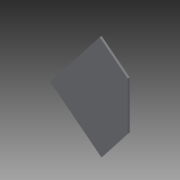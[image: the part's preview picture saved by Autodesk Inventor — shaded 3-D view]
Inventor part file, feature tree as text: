
AUTODESK INVENTOR PART (.ipt)
format: ipt  version: 2015 (Build 190159000, 159)  size: 75,776 bytes
history: native  units: in
note: dims shown in document units (in); Inventor stores cm internally (conversion verified against a paired STEP export)
features: plane x1, extrude x1, sketch x1, reference x1
ambient origin geometry x8: Origin, YZ Plane, XZ Plane, XY Plane, X Axis, Y Axis, Z Axis, Center Point
bodies: Solid1 (feature_tree)
feature tree (4):
  plane  "Work Plane1"
  extrude  "Extrusion1"  Depth=0.125in
  sketch  "Sketch1"  dims[d0=4.0in d1=1.7in d2=0.125in d3=0.0in]
  reference  "Reference1"
